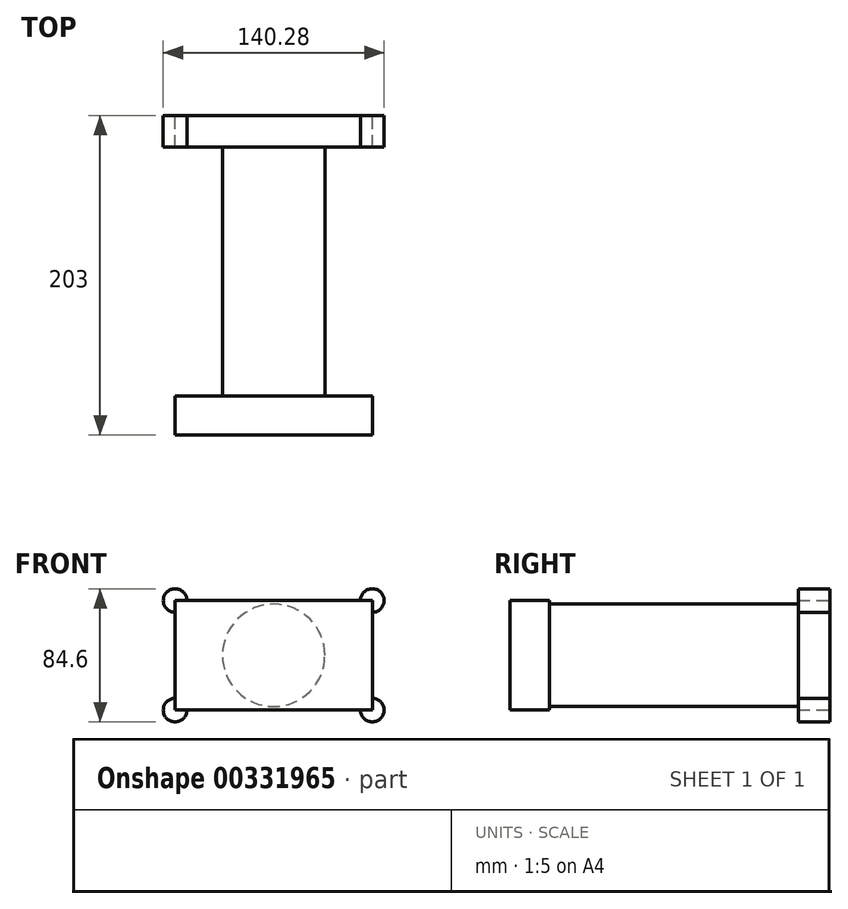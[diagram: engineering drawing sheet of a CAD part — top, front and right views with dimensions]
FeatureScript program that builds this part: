
annotation { "Feature Type Name" : "Feature", "Feature Type Description" : "" }
export const myFeature = defineFeature(function(context is Context, id is Id, definition is map)
    precondition{}
    {
        {
            var Q0;
            Q0=qCreatedBy(makeId("Front.planeOp"),FACE);
            var sketch = newSketch(context, id + "F0", { "sketchPlane" : qUnion([Q0])});
            skLineSegment(sketch, "E0.bottom", {"start": v(55.14, 34.8) * mm, "end": v(-55.14, 34.8) * mm});
            skLineSegment(sketch, "E0.top", {"start": v(55.14, -34.8) * mm, "end": v(-55.14, -34.8) * mm});
            skLineSegment(sketch, "E0.left", {"start": v(62.64, 27.3) * mm, "end": v(62.64, -27.3) * mm});
            skLineSegment(sketch, "E0.right", {"start": v(-62.64, 27.3) * mm, "end": v(-62.64, -27.3) * mm});
            skPoint(sketch, "E0.middle", {"position": v(0, 0) * mm});
            skArc(sketch, "E1", {"start": v(62.64, 27.3) * mm, "mid": v(67.94, 40.1) * mm, "end": v(55.14, 34.8) * mm});
            skArc(sketch, "E2", {"start": v(-55.14, 34.8) * mm, "mid": v(-67.94, 40.1) * mm, "end": v(-62.64, 27.3) * mm});
            skArc(sketch, "E3", {"start": v(-62.64, -27.3) * mm, "mid": v(-67.94, -40.1) * mm, "end": v(-55.14, -34.8) * mm});
            skArc(sketch, "E4", {"start": v(55.14, -34.8) * mm, "mid": v(67.94, -40.1) * mm, "end": v(62.64, -27.3) * mm});
            skSolve(sketch);
        }
        {
            var Q0;
            Q0=makeQuery(id+"F0.imprint","IMPRINT",FACE,{"disambiguationData":[TD([[makeQuery(id+"F0.imprint","IMPRINT",EDGE,{"derivedFrom":sQuery(id+"F0.wireOp",EDGE,"E0.bottom")}),1.0]])]});
            var Q1;
            Q1=sQuery(id+"F0.wireOp",EDGE,"E0.bottom");
            extrude(context, id + "F1", {"entities" : qUnion([Q0]), "surfaceEntities" : qUnion([Q1]), "depth" : 20 * mm});
        }
        {
            var Q0;
            Q0=makeQuery(id+"F1.opExtrude","CAP_FACE",FACE,{"disambiguationData":[OSD([sQuery(id+"F0.wireOp",EDGE,"E0.bottom"),sQuery(id+"F0.wireOp",EDGE,"E0.top"),sQuery(id+"F0.wireOp",EDGE,"E0.left"),sQuery(id+"F0.wireOp",EDGE,"E0.right"),sQuery(id+"F0.wireOp",EDGE,"E1"),sQuery(id+"F0.wireOp",EDGE,"E2"),sQuery(id+"F0.wireOp",EDGE,"E3"),sQuery(id+"F0.wireOp",EDGE,"E4")])],"isStart":false});
            var sketch = newSketch(context, id + "F2", { "sketchPlane" : qUnion([Q0])});
            skCircle(sketch, "E5", {"center": v(0, 0) * mm, "radius": 32.5 * mm});
            skSolve(sketch);
        }
        {
            var Q0;
            Q0=makeQuery(id+"F2.imprint","IMPRINT",FACE,{"disambiguationData":[TD([[makeQuery(id+"F2.imprint","IMPRINT",EDGE,{"derivedFrom":sQuery(id+"F2.wireOp",EDGE,"E5")}),1.0]])]});
            var Q1;
            Q1=sQuery(id+"F2.wireOp",EDGE,"E5");
            extrude(context, id + "F3", {"entities" : qUnion([Q0]), "operationType" : NewBodyOperationType.ADD, "surfaceEntities" : qUnion([Q1]), "depth" : 158 * mm});
        }
        {
            var Q0;
            Q0=makeQuery(id+"F3.opExtrude","CAP_FACE",FACE,{"disambiguationData":[OSD([sQuery(id+"F2.wireOp",EDGE,"E5")])],"isStart":false});
            var sketch = newSketch(context, id + "F4", { "sketchPlane" : qUnion([Q0])});
            skLineSegment(sketch, "E6.bottom", {"start": v(62.64, 34.8) * mm, "end": v(-62.64, 34.8) * mm});
            skLineSegment(sketch, "E6.top", {"start": v(62.64, -34.8) * mm, "end": v(-62.64, -34.8) * mm});
            skLineSegment(sketch, "E6.left", {"start": v(62.64, 34.8) * mm, "end": v(62.64, -34.8) * mm});
            skLineSegment(sketch, "E6.right", {"start": v(-62.64, 34.8) * mm, "end": v(-62.64, -34.8) * mm});
            skPoint(sketch, "E6.middle", {"position": v(0, 0) * mm});
            skSolve(sketch);
        }
        {
            var Q0;
            Q0 = qSketchRegion(id + "F4", true);
            extrude(context, id + "F5", {"entities" : qUnion([Q0]), "operationType" : NewBodyOperationType.ADD, "depth" : 25 * mm});
        }
    });
